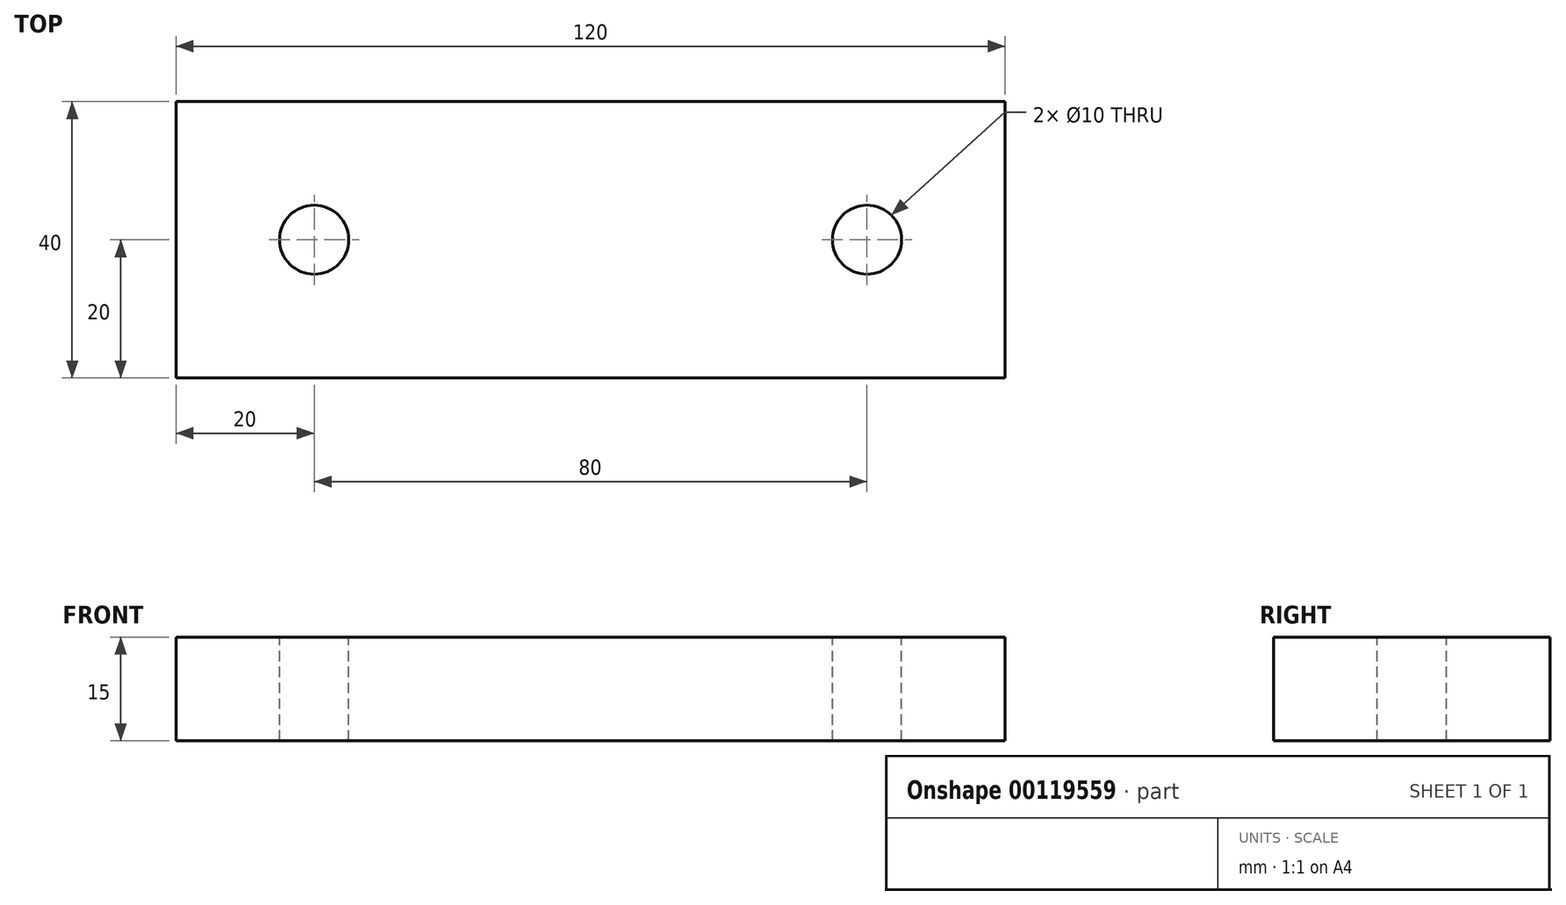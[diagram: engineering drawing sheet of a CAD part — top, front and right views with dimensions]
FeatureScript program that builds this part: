
annotation { "Feature Type Name" : "Feature", "Feature Type Description" : "" }
export const myFeature = defineFeature(function(context is Context, id is Id, definition is map)
    precondition{}
    {
        {
            var Q0;
            Q0=qCreatedBy(makeId("Top.planeOp"),FACE);
            var sketch = newSketch(context, id + "F0", { "sketchPlane" : qUnion([Q0])});
            skLineSegment(sketch, "E0.bottom", {"start": v(0, 0) * mm, "end": v(120, 0) * mm});
            skLineSegment(sketch, "E0.top", {"start": v(0, 40) * mm, "end": v(120, 40) * mm});
            skLineSegment(sketch, "E0.left", {"start": v(0, 0) * mm, "end": v(0, 40) * mm});
            skLineSegment(sketch, "E0.right", {"start": v(120, 0) * mm, "end": v(120, 40) * mm});
            skLineSegment(sketch, "E1", {"start": v(20, 40) * mm, "end": v(20, 0) * mm, "construction": true});
            skLineSegment(sketch, "E2", {"start": v(100, 40) * mm, "end": v(100, 0) * mm, "construction": true});
            skLineSegment(sketch, "E3", {"start": v(0, 20) * mm, "end": v(120, 20) * mm, "construction": true});
            skSolve(sketch);
        }
        {
            var Q0;
            Q0=makeQuery(id+"F0.imprint","IMPRINT",FACE,{"disambiguationData":[TD([[makeQuery(id+"F0.imprint","IMPRINT",EDGE,{"derivedFrom":sQuery(id+"F0.wireOp",EDGE,"E0.bottom")}),1.0]])]});
            extrude(context, id + "F1", {"entities" : qUnion([Q0]), "depth" : 15 * mm});
        }
        {
            var Q0;
            Q0=makeQuery(id+"F1.opExtrude","CAP_FACE",FACE,{"disambiguationData":[OSD([sQuery(id+"F0.wireOp",EDGE,"E0.bottom"),sQuery(id+"F0.wireOp",EDGE,"E0.top"),sQuery(id+"F0.wireOp",EDGE,"E0.left"),sQuery(id+"F0.wireOp",EDGE,"E0.right")])],"isStart":false});
            var sketch = newSketch(context, id + "F2", { "sketchPlane" : qUnion([Q0])});
            skCircle(sketch, "E4", {"center": v(20, 20) * mm, "radius": 5 * mm});
            skCircle(sketch, "E5", {"center": v(100, 20) * mm, "radius": 5 * mm});
            skSolve(sketch);
        }
        {
            var Q0;
            Q0=makeQuery(id+"F2.imprint","IMPRINT",FACE,{"disambiguationData":[TD([[makeQuery(id+"F2.imprint","IMPRINT",EDGE,{"derivedFrom":sQuery(id+"F2.wireOp",EDGE,"E4")}),1.0]])]});
            var Q1;
            Q1=makeQuery(id+"F2.imprint","IMPRINT",FACE,{"disambiguationData":[TD([[makeQuery(id+"F2.imprint","IMPRINT",EDGE,{"derivedFrom":sQuery(id+"F2.wireOp",EDGE,"E5")}),1.0]])]});
            extrude(context, id + "F3", {"entities" : qUnion([Q0, Q1]), "operationType" : NewBodyOperationType.REMOVE, "endBound" : BoundingType.THROUGH_ALL, "oppositeDirection" : true, "depth" : 25 * mm});
        }
    });
